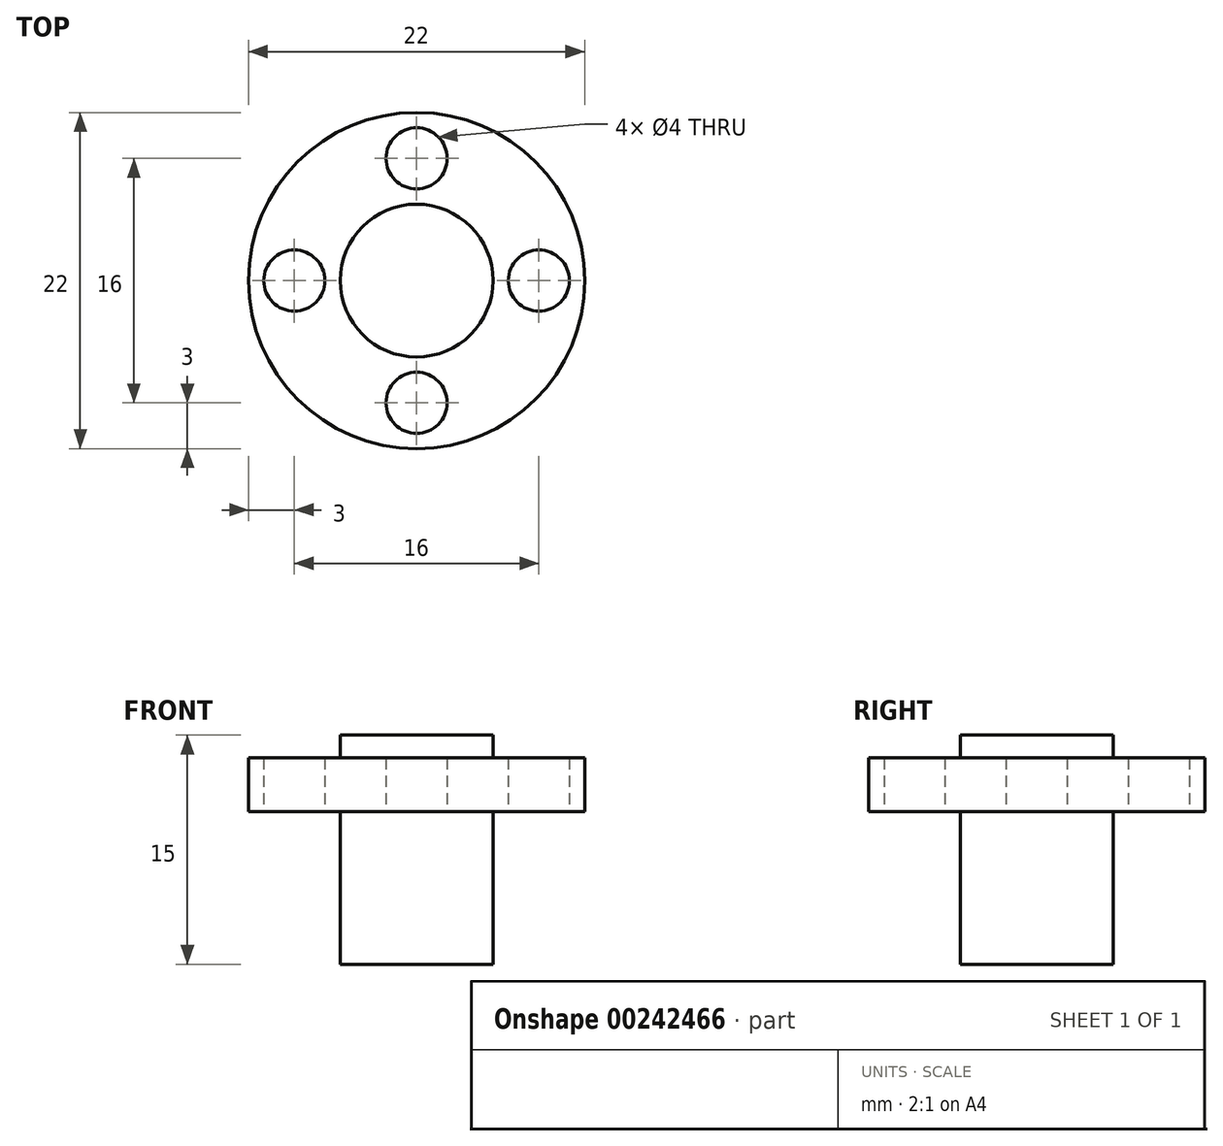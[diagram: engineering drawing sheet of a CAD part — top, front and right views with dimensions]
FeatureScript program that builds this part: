
annotation { "Feature Type Name" : "Feature", "Feature Type Description" : "" }
export const myFeature = defineFeature(function(context is Context, id is Id, definition is map)
    precondition{}
    {
        {
            var Q0;
            Q0=qCreatedBy(makeId("Top.planeOp"),FACE);
            var sketch = newSketch(context, id + "F0", { "sketchPlane" : qUnion([Q0])});
            skCircle(sketch, "E0", {"center": v(0, 0) * mm, "radius": 11 * mm});
            skCircle(sketch, "E1", {"center": v(0, 0) * mm, "radius": 8 * mm, "construction": true});
            skCircle(sketch, "E2", {"center": v(0, 8) * mm, "radius": 2 * mm});
            skCircle(sketch, "E3", {"center": v(-8, 0) * mm, "radius": 2 * mm});
            skCircle(sketch, "E4", {"center": v(0, -8) * mm, "radius": 2 * mm});
            skCircle(sketch, "E5", {"center": v(8, 0) * mm, "radius": 2 * mm});
            skSolve(sketch);
        }
        {
            var Q0;
            Q0=makeQuery(id+"F0.imprint","IMPRINT",FACE,{"disambiguationData":[TD([[makeQuery(id+"F0.imprint","IMPRINT",EDGE,{"derivedFrom":sQuery(id+"F0.wireOp",EDGE,"E0")}),1.0]])]});
            extrude(context, id + "F1", {"entities" : qUnion([Q0]), "depth" : 3.5 * mm});
        }
        {
            var Q0;
            Q0=makeQuery(id+"F1.opExtrude","CAP_FACE",FACE,{"disambiguationData":[OSD([sQuery(id+"F0.wireOp",EDGE,"E0")])],"isStart":false});
            var sketch = newSketch(context, id + "F2", { "sketchPlane" : qUnion([Q0])});
            skCircle(sketch, "E6", {"center": v(0, 0) * mm, "radius": 5 * mm});
            skSolve(sketch);
        }
        {
            var Q0;
            Q0=makeQuery(id+"F2.imprint","IMPRINT",FACE,{"disambiguationData":[TD([[makeQuery(id+"F2.imprint","IMPRINT",EDGE,{"derivedFrom":sQuery(id+"F2.wireOp",EDGE,"E6")}),1.0]])]});
            extrude(context, id + "F3", {"entities" : qUnion([Q0]), "operationType" : NewBodyOperationType.ADD, "depth" : 1.5 * mm});
        }
        {
            var Q0;
            Q0=makeQuery(id+"F1.opExtrude","CAP_FACE",FACE,{"disambiguationData":[OSD([sQuery(id+"F0.wireOp",EDGE,"E0")])],"isStart":true});
            var sketch = newSketch(context, id + "F4", { "sketchPlane" : qUnion([Q0])});
            skCircle(sketch, "E7", {"center": v(0, 0) * mm, "radius": 5 * mm});
            skSolve(sketch);
        }
        {
            var Q0;
            Q0=makeQuery(id+"F4.imprint","IMPRINT",FACE,{"disambiguationData":[TD([[makeQuery(id+"F4.imprint","IMPRINT",EDGE,{"derivedFrom":sQuery(id+"F4.wireOp",EDGE,"E7")}),1.0]])]});
            extrude(context, id + "F5", {"entities" : qUnion([Q0]), "operationType" : NewBodyOperationType.ADD, "depth" : 10 * mm});
        }
    });
